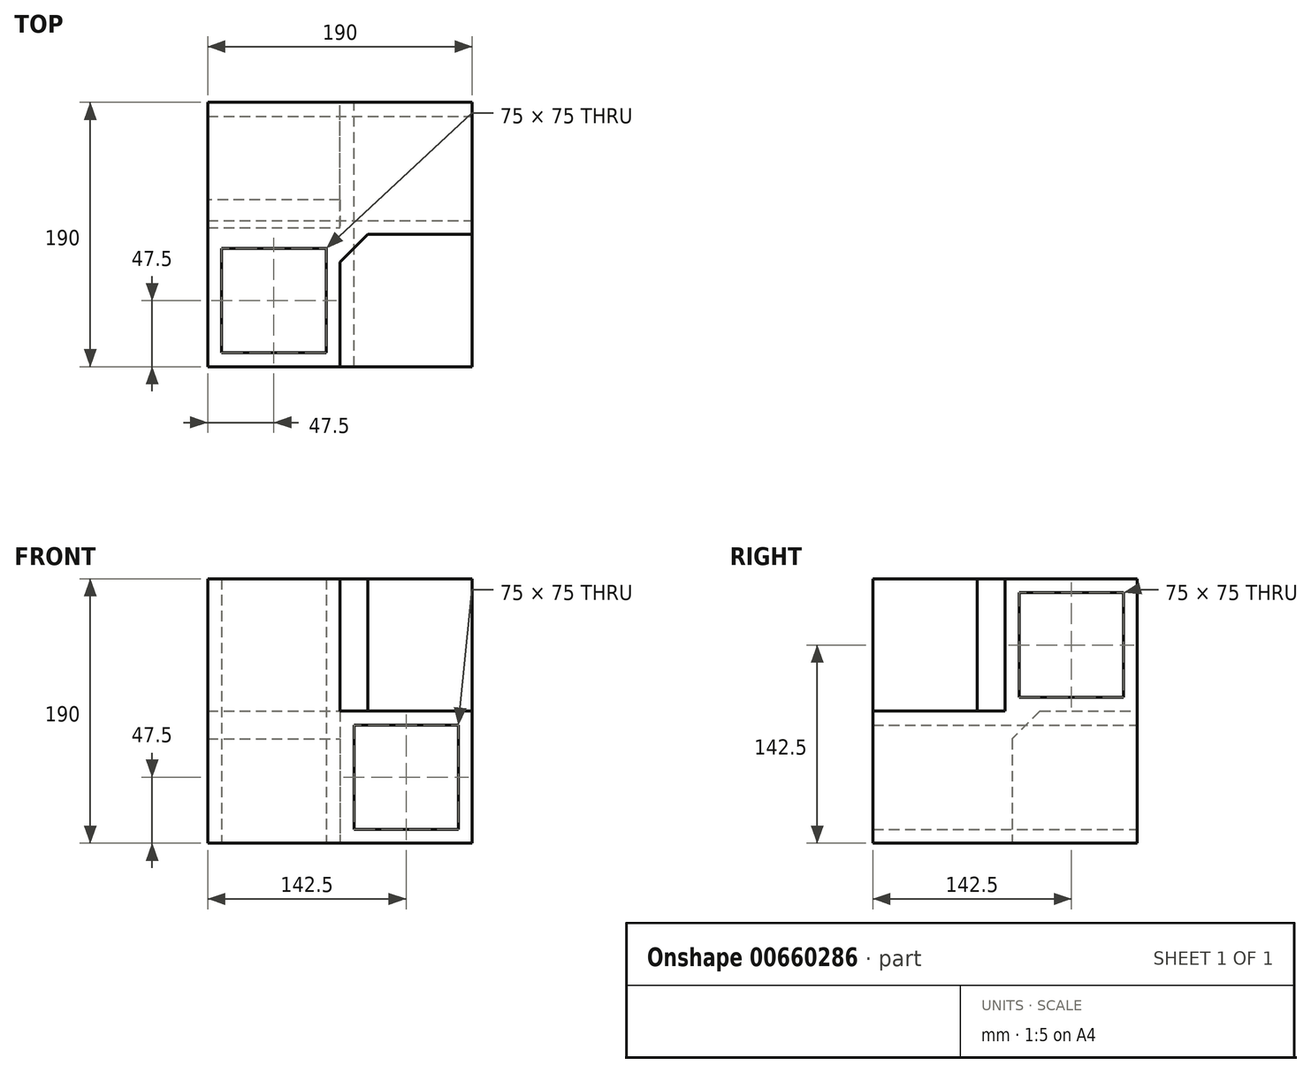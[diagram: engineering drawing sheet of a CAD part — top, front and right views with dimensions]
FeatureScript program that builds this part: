
annotation { "Feature Type Name" : "Feature", "Feature Type Description" : "" }
export const myFeature = defineFeature(function(context is Context, id is Id, definition is map)
    precondition{}
    {
        {
            var Q0;
            Q0=qCreatedBy(makeId("Front.planeOp"),FACE);
            var sketch = newSketch(context, id + "F0", { "sketchPlane" : qUnion([Q0])});
            skLineSegment(sketch, "E0.bottom", {"start": v(37.5, 37.5) * mm, "end": v(-37.5, 37.5) * mm});
            skLineSegment(sketch, "E0.top", {"start": v(37.5, -37.5) * mm, "end": v(-37.5, -37.5) * mm});
            skLineSegment(sketch, "E0.left", {"start": v(37.5, 37.5) * mm, "end": v(37.5, -37.5) * mm});
            skLineSegment(sketch, "E0.right", {"start": v(-37.5, 37.5) * mm, "end": v(-37.5, -37.5) * mm});
            skPoint(sketch, "E0.middle", {"position": v(0, 0) * mm});
            skLineSegment(sketch, "E1.bottom", {"start": v(47.5, 47.5) * mm, "end": v(-47.5, 47.5) * mm});
            skLineSegment(sketch, "E1.top", {"start": v(47.5, -47.5) * mm, "end": v(-47.5, -47.5) * mm});
            skLineSegment(sketch, "E1.left", {"start": v(47.5, 47.5) * mm, "end": v(47.5, -47.5) * mm});
            skLineSegment(sketch, "E1.right", {"start": v(-47.5, 47.5) * mm, "end": v(-47.5, -47.5) * mm});
            skSolve(sketch);
        }
        {
            var Q0;
            Q0 = qSketchRegion(id + "F0", true);
            extrude(context, id + "F1", {"entities" : qUnion([Q0]), "depth" : 190 * mm, "offsetDistance" : 25 * mm});
        }
        {
            var Q0;
            Q0=makeQuery(id+"F1.opExtrude","SWEPT_FACE",FACE,{"disambiguationData":[OSD([sQuery(id+"F0.wireOp",EDGE,"E1.left")])]});
            var sketch = newSketch(context, id + "F2", { "sketchPlane" : qUnion([Q0])});
            skLineSegment(sketch, "E2.bottom", {"start": v(0, 47.5) * mm, "end": v(-95, 47.5) * mm});
            skLineSegment(sketch, "E2.top", {"start": v(0, 142.5) * mm, "end": v(-95, 142.5) * mm});
            skLineSegment(sketch, "E2.left", {"start": v(0, 47.5) * mm, "end": v(0, 142.5) * mm});
            skLineSegment(sketch, "E2.right", {"start": v(-95, 47.5) * mm, "end": v(-95, 142.5) * mm});
            skLineSegment(sketch, "E3.0", {"start": v(-10, 132.5) * mm, "end": v(-85, 132.5) * mm});
            skLineSegment(sketch, "E3.1", {"start": v(-10, 57.5) * mm, "end": v(-10, 132.5) * mm});
            skLineSegment(sketch, "E3.2", {"start": v(-10, 57.5) * mm, "end": v(-85, 57.5) * mm});
            skLineSegment(sketch, "E3.3", {"start": v(-85, 57.5) * mm, "end": v(-85, 132.5) * mm});
            skSolve(sketch);
        }
        {
            var Q0;
            Q0 = qSketchRegion(id + "F2", true);
            var Q1;
            Q1=makeQuery(id+"F2.imprint","IMPRINT",FACE,{"disambiguationData":[TD([[makeQuery(id+"F2.imprint","IMPRINT",EDGE,{"derivedFrom":sQuery(id+"F2.wireOp",EDGE,"E2.bottom")}),1.0]])]});
            extrude(context, id + "F3", {"entities" : qUnion([Q0, Q1]), "operationType" : NewBodyOperationType.ADD, "oppositeDirection" : true, "depth" : 190 * mm, "offsetDistance" : 25 * mm});
        }
        {
            var Q0;
            Q0=makeQuery(id+"F1.opExtrude","SWEPT_FACE",FACE,{"disambiguationData":[OSD([sQuery(id+"F0.wireOp",EDGE,"E1.top")])]});
            var sketch = newSketch(context, id + "F4", { "sketchPlane" : qUnion([Q0])});
            skLineSegment(sketch, "E4.bottom", {"start": v(-47.5, 190) * mm, "end": v(-142.5, 190) * mm});
            skLineSegment(sketch, "E4.left", {"start": v(-47.5, 190) * mm, "end": v(-47.5, 95) * mm});
            skLineSegment(sketch, "E4.right", {"start": v(-142.5, 190) * mm, "end": v(-142.5, 95) * mm});
            skLineSegment(sketch, "E5.0", {"start": v(-132.5, 180) * mm, "end": v(-132.5, 105) * mm});
            skLineSegment(sketch, "E5.1", {"start": v(-57.5, 180) * mm, "end": v(-132.5, 180) * mm});
            skLineSegment(sketch, "E5.2", {"start": v(-57.5, 180) * mm, "end": v(-57.5, 105) * mm});
            skLineSegment(sketch, "E5.3", {"start": v(-57.5, 105) * mm, "end": v(-132.5, 105) * mm});
            skLineSegment(sketch, "E6", {"start": v(-142.5, 95) * mm, "end": v(-142.5, 90) * mm});
            skLineSegment(sketch, "E7", {"start": v(-142.5, 90) * mm, "end": v(-47.5, 90) * mm});
            skLineSegment(sketch, "E8", {"start": v(-47.5, 90) * mm, "end": v(-47.5, 95) * mm});
            skSolve(sketch);
        }
        {
            var Q0;
            Q0 = qSketchRegion(id + "F4", true);
            extrude(context, id + "F5", {"entities" : qUnion([Q0]), "operationType" : NewBodyOperationType.ADD, "oppositeDirection" : true, "depth" : 190 * mm, "offsetDistance" : 25 * mm});
        }
        {
            var Q0;
            {var subQ0=sQuery(id+"F0.wireOp",EDGE,"E1.bottom");var subQ1=sQuery(id+"F2.wireOp",EDGE,"E2.right");Q0=makeQuery(id+"F3.boolean.opBoolean","SPLIT",EDGE,{"disambiguationData":[topologyDisambiguationEdgeConnected([makeQuery(id+"F1.opExtrude","SWEPT_FACE",FACE,{"disambiguationData":[OSD([subQ0])]})])],"derivedFrom":makeQuery(id+"F3.opExtrude","SWEPT_EDGE",EDGE,{"disambiguationData":[OSD([subQ0,sQuery(id+"F0.wireOp",EDGE,"E1.left"),sQuery(id+"F2.wireOp",EDGE,"E2.bottom"),subQ1])]})});}
            var Q1;
            {var subQ0=sQuery(id+"F0.wireOp",EDGE,"E1.bottom");var subQ1=sQuery(id+"F0.wireOp",EDGE,"E1.right");Q1=makeQuery(id+"F3.boolean.opBoolean","SPLIT",EDGE,{"disambiguationData":[topologyDisambiguationEdgeConnected([makeQuery(id+"F1.opExtrude","SWEPT_FACE",FACE,{"disambiguationData":[OSD([subQ0])]})])],"derivedFrom":makeQuery(id+"F1.opExtrude","SWEPT_EDGE",EDGE,{"disambiguationData":[OSD([subQ0,subQ1])]})});}
            var Q2;
            Q2=makeQuery(id+"F5.boolean.opBoolean","INTERSECT",EDGE,{"derivedFrom":[makeQuery(id+"F3.opExtrude","SWEPT_FACE",FACE,{"disambiguationData":[OSD([sQuery(id+"F2.wireOp",EDGE,"E2.right")])]}),makeQuery(id+"F5.opExtrude","SWEPT_FACE",FACE,{"disambiguationData":[OSD([sQuery(id+"F4.wireOp",EDGE,"E4.left"),sQuery(id+"F4.wireOp",EDGE,"E8")])]})]});
            var Q3;
            Q3=makeQuery(id+"F5.boolean.opBoolean","INTERSECT",EDGE,{"derivedFrom":[makeQuery(id+"F3.opExtrude","SWEPT_FACE",FACE,{"disambiguationData":[OSD([sQuery(id+"F2.wireOp",EDGE,"E2.bottom")])]}),makeQuery(id+"F5.opExtrude","SWEPT_FACE",FACE,{"disambiguationData":[OSD([sQuery(id+"F4.wireOp",EDGE,"E7")])]})]});
            var Q4;
            Q4=makeQuery(id+"F5.opExtrude","SWEPT_EDGE",EDGE,{"disambiguationData":[OSD([sQuery(id+"F0.wireOp",EDGE,"E1.top"),sQuery(id+"F0.wireOp",EDGE,"E1.right"),sQuery(id+"F4.wireOp",EDGE,"E7"),sQuery(id+"F4.wireOp",EDGE,"E8")])]});
            var Q5;
            {var subQ0=sQuery(id+"F0.wireOp",EDGE,"E1.right");Q5=makeQuery(id+"F3.boolean.opBoolean","SPLIT",EDGE,{"disambiguationData":[topologyDisambiguationEdgeConnected([makeQuery(id+"F3.opExtrude","SWEPT_FACE",FACE,{"disambiguationData":[OSD([sQuery(id+"F2.wireOp",EDGE,"E2.bottom")])]})])],"derivedFrom":makeQuery(id+"F1.opExtrude","SWEPT_EDGE",EDGE,{"disambiguationData":[OSD([sQuery(id+"F0.wireOp",EDGE,"E1.bottom"),subQ0])]})});}
            chamfer(context, id + "F6", {"entities" : qUnion([Q0, Q1, Q2, Q3, Q4, Q5]), "width" : 20 * mm, "tangentPropagation" : true});
        }
    });
